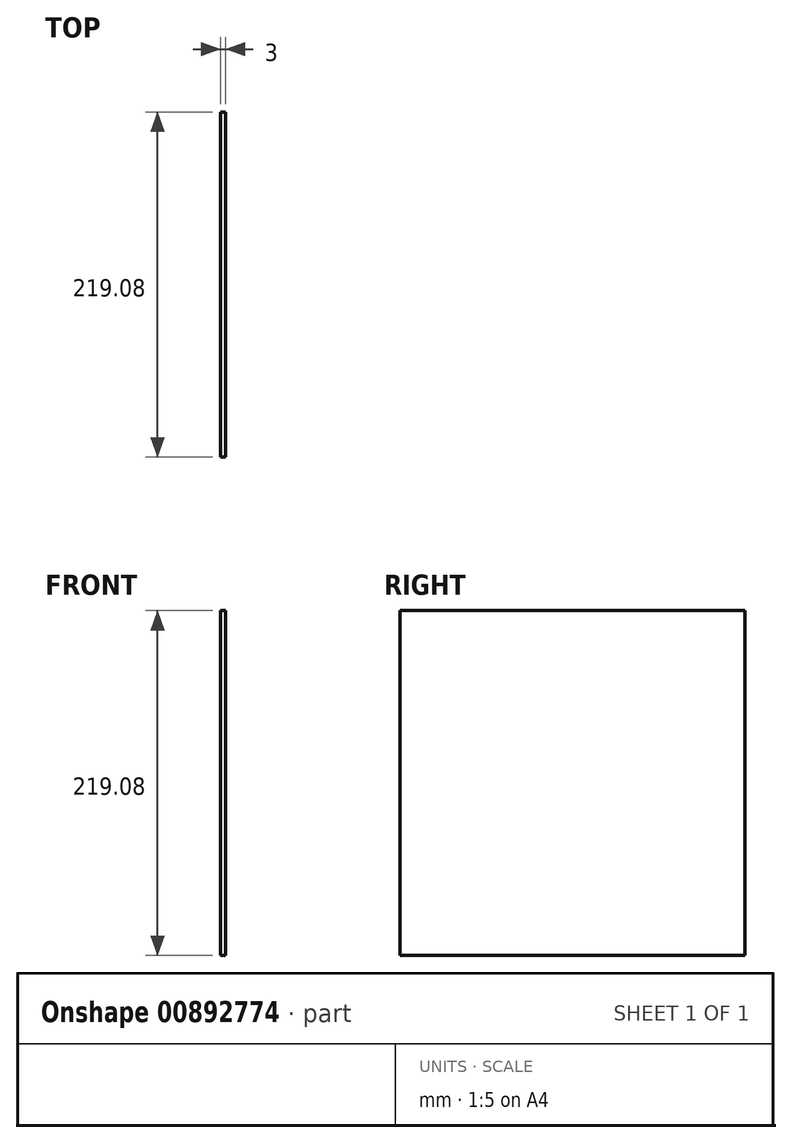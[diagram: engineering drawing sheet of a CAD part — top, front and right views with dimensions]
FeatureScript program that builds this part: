
annotation { "Feature Type Name" : "Feature", "Feature Type Description" : "" }
export const myFeature = defineFeature(function(context is Context, id is Id, definition is map)
    precondition{}
    {
        {
            var Q0;
            Q0=qCreatedBy(makeId("Right.planeOp"),FACE);
            var sketch = newSketch(context, id + "F0", { "sketchPlane" : qUnion([Q0])});
            skLineSegment(sketch, "E0.bottom", {"start": v(113.93, 109.54) * mm, "end": v(-105.15, 109.54) * mm});
            skLineSegment(sketch, "E0.top", {"start": v(113.93, -109.54) * mm, "end": v(-105.15, -109.54) * mm});
            skLineSegment(sketch, "E0.left", {"start": v(113.93, 109.54) * mm, "end": v(113.93, -109.54) * mm});
            skLineSegment(sketch, "E0.right", {"start": v(-105.15, 109.54) * mm, "end": v(-105.15, -109.54) * mm});
            skPoint(sketch, "E0.middle", {"position": v(4.4, 0) * mm});
            skSolve(sketch);
        }
        {
            var Q0;
            Q0 = qSketchRegion(id + "F0", true);
            extrude(context, id + "F1", {"entities" : qUnion([Q0]), "depth" : 3 * mm, "offsetDistance" : 25.4 * mm});
        }
    });
